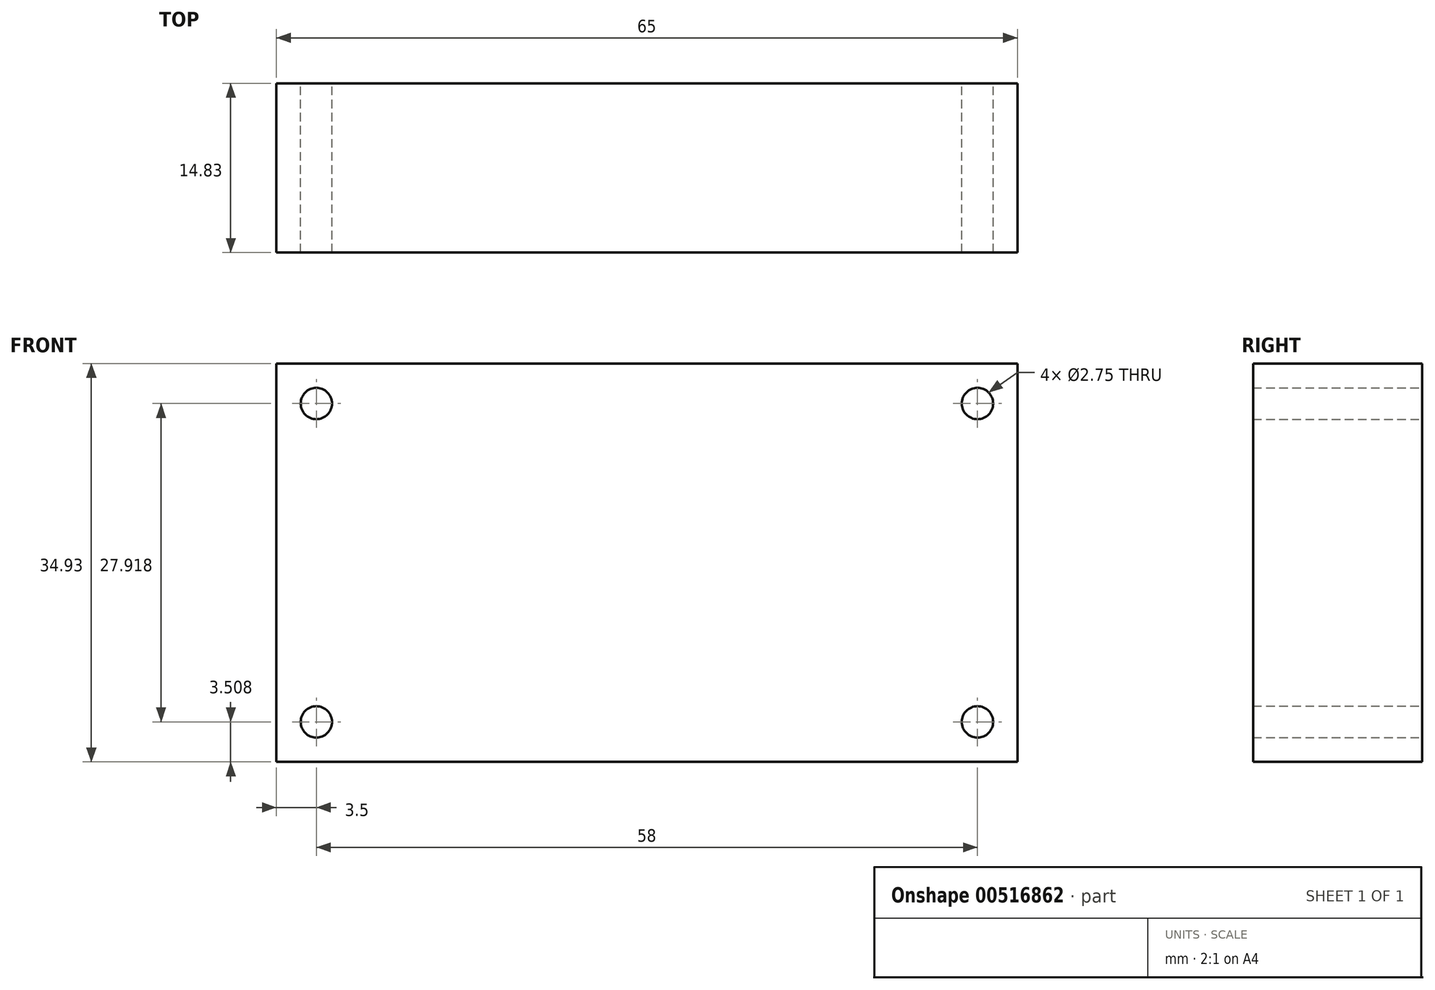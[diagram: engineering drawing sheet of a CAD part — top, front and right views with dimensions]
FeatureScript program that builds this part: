
annotation { "Feature Type Name" : "Feature", "Feature Type Description" : "" }
export const myFeature = defineFeature(function(context is Context, id is Id, definition is map)
    precondition{}
    {
        {
            var Q0;
            Q0=qCreatedBy(makeId("Front.planeOp"),FACE);
            var sketch = newSketch(context, id + "F0", { "sketchPlane" : qUnion([Q0])});
            skLineSegment(sketch, "E0.bottom", {"start": v(-31.18, 21.02) * mm, "end": v(33.82, 21.02) * mm});
            skLineSegment(sketch, "E0.top", {"start": v(-31.18, -13.9) * mm, "end": v(33.82, -13.9) * mm});
            skLineSegment(sketch, "E0.left", {"start": v(-31.18, 21.02) * mm, "end": v(-31.18, -13.9) * mm});
            skLineSegment(sketch, "E0.right", {"start": v(33.82, 21.02) * mm, "end": v(33.82, -13.9) * mm});
            skCircle(sketch, "E1", {"center": v(-27.68, 17.52) * mm, "radius": 1.37 * mm});
            skCircle(sketch, "E2", {"center": v(30.32, 17.52) * mm, "radius": 1.37 * mm});
            skCircle(sketch, "E3", {"center": v(-27.68, -10.4) * mm, "radius": 1.37 * mm});
            skCircle(sketch, "E4", {"center": v(30.32, -10.4) * mm, "radius": 1.37 * mm});
            skSolve(sketch);
        }
        {
            var Q0;
            Q0=makeQuery(id+"F0.imprint","IMPRINT",FACE,{"disambiguationData":[TD([[makeQuery(id+"F0.imprint","IMPRINT",EDGE,{"derivedFrom":sQuery(id+"F0.wireOp",EDGE,"E0.bottom")}),-1.0]])]});
            extrude(context, id + "F1", {"entities" : qUnion([Q0]), "depth" : 14.83 * mm, "offsetDistance" : 25.4 * mm});
        }
    });
